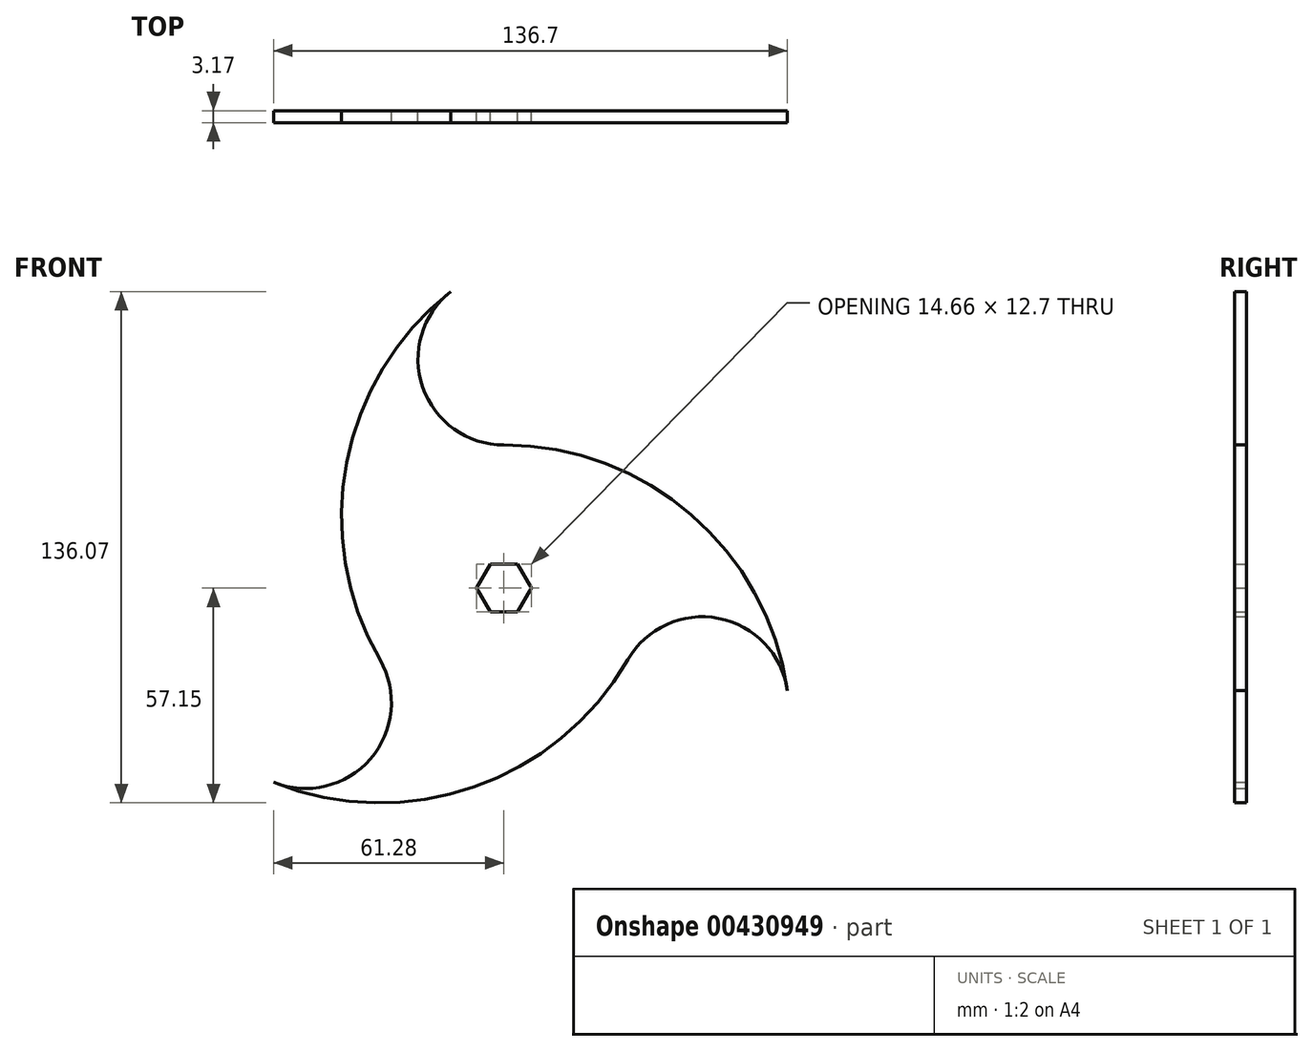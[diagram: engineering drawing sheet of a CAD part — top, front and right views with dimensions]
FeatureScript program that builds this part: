
annotation { "Feature Type Name" : "Feature", "Feature Type Description" : "" }
export const myFeature = defineFeature(function(context is Context, id is Id, definition is map)
    precondition{}
    {
        {
            var Q0;
            Q0=qCreatedBy(makeId("Front.planeOp"),FACE);
            var sketch = newSketch(context, id + "F0", { "sketchPlane" : qUnion([Q0])});
            skCircle(sketch, "E0.cCircle", {"center": v(0, 0) * mm, "radius": 6.35 * mm, "construction": true});
            skLineSegment(sketch, "E0.0", {"start": v(7.33, 0) * mm, "end": v(3.67, -6.35) * mm});
            skLineSegment(sketch, "E0.1", {"start": v(3.67, -6.35) * mm, "end": v(-3.67, -6.35) * mm});
            skLineSegment(sketch, "E0.2", {"start": v(-3.67, -6.35) * mm, "end": v(-7.33, 0) * mm});
            skLineSegment(sketch, "E0.3", {"start": v(-7.33, 0) * mm, "end": v(-3.67, 6.35) * mm});
            skLineSegment(sketch, "E0.4", {"start": v(-3.67, 6.35) * mm, "end": v(3.67, 6.35) * mm});
            skLineSegment(sketch, "E0.5", {"start": v(3.67, 6.35) * mm, "end": v(7.33, 0) * mm});
            skPoint(sketch, "E0.0.midPoint", {"position": v(5.5, -3.18) * mm});
            skCircle(sketch, "E1", {"center": v(0, 0) * mm, "radius": 38.1 * mm});
            skCircle(sketch, "E2.cCircle", {"center": v(0, 0) * mm, "radius": 38.1 * mm, "construction": true});
            skLineSegment(sketch, "E2.0", {"start": v(33, -19.05) * mm, "end": v(-33, -19.05) * mm, "construction": true});
            skLineSegment(sketch, "E2.1", {"start": v(-33, -19.05) * mm, "end": v(0, 38.1) * mm, "construction": true});
            skLineSegment(sketch, "E2.2", {"start": v(0, 38.1) * mm, "end": v(33, -19.05) * mm, "construction": true});
            skCircle(sketch, "E3", {"center": v(0, -38.1) * mm, "radius": 76.2 * mm});
            skCircle(sketch, "E4", {"center": v(52.8, -30.48) * mm, "radius": 22.86 * mm});
            skCircle(sketch, "E5.1.0", {"center": v(0, 60.96) * mm, "radius": 22.86 * mm});
            skCircle(sketch, "E5.1.1", {"center": v(33, 19.05) * mm, "radius": 76.2 * mm});
            skCircle(sketch, "E5.2.0", {"center": v(-52.8, -30.48) * mm, "radius": 22.86 * mm});
            skCircle(sketch, "E5.2.1", {"center": v(-33, 19.05) * mm, "radius": 76.2 * mm});
            skSolve(sketch);
        }
        {
            var Q0;
            {var subQ0=sQuery(id+"F0.wireOp",EDGE,"E5.1.0");var subQ1=sQuery(id+"F0.wireOp",EDGE,"E1");var subQ2=makeQuery(id+"F0.imprint","INTERSECT",VERTEX,{"derivedFrom":[subQ1,subQ0]});Q0=makeQuery(id+"F0.imprint","IMPRINT",FACE,{"disambiguationData":[TD([[makeQuery(id+"F0.imprint","IMPRINT",EDGE,{"disambiguationData":[TD([[subQ2,-1.0]])],"derivedFrom":subQ1}),-1.0]])]});}
            var Q1;
            {var subQ0=sQuery(id+"F0.wireOp",EDGE,"E5.2.0");var subQ1=sQuery(id+"F0.wireOp",EDGE,"E1");var subQ2=makeQuery(id+"F0.imprint","INTERSECT",VERTEX,{"derivedFrom":[subQ1,subQ0]});Q1=makeQuery(id+"F0.imprint","IMPRINT",FACE,{"disambiguationData":[TD([[makeQuery(id+"F0.imprint","IMPRINT",EDGE,{"disambiguationData":[TD([[subQ2,-1.0]])],"derivedFrom":subQ1}),-1.0]])]});}
            var Q2;
            {var subQ0=sQuery(id+"F0.wireOp",EDGE,"E3");var subQ1=sQuery(id+"F0.wireOp",EDGE,"E1");var subQ2=makeQuery(id+"F0.imprint","INTERSECT",VERTEX,{"derivedFrom":[subQ1,subQ0]});Q2=makeQuery(id+"F0.imprint","IMPRINT",FACE,{"disambiguationData":[TD([[makeQuery(id+"F0.imprint","IMPRINT",EDGE,{"disambiguationData":[TD([[subQ2,1.0]])],"derivedFrom":subQ1}),-1.0]])]});}
            var Q3;
            Q3=makeQuery(id+"F0.imprint","IMPRINT",FACE,{"disambiguationData":[TD([[makeQuery(id+"F0.imprint","IMPRINT",EDGE,{"derivedFrom":sQuery(id+"F0.wireOp",EDGE,"E0.0")}),1.0]])]});
            var Q4;
            {var subQ0=sQuery(id+"F0.wireOp",EDGE,"E5.1.0");var subQ1=sQuery(id+"F0.wireOp",EDGE,"E3");var subQ2=makeQuery(id+"F0.imprint","INTERSECT",VERTEX,{"disambiguationData":[OD(1.0)],"derivedFrom":[subQ1,subQ0]});Q4=makeQuery(id+"F0.imprint","IMPRINT",FACE,{"disambiguationData":[TD([[makeQuery(id+"F0.imprint","IMPRINT",EDGE,{"disambiguationData":[TD([[subQ2,-1.0]])],"derivedFrom":subQ1}),-1.0]])]});}
            var Q5;
            {var subQ0=sQuery(id+"F0.wireOp",EDGE,"E4");var subQ1=sQuery(id+"F0.wireOp",EDGE,"E3");var subQ2=makeQuery(id+"F0.imprint","INTERSECT",VERTEX,{"derivedFrom":[subQ1,subQ0]});Q5=makeQuery(id+"F0.imprint","IMPRINT",FACE,{"disambiguationData":[TD([[makeQuery(id+"F0.imprint","IMPRINT",EDGE,{"disambiguationData":[TD([[subQ2,-1.0]])],"derivedFrom":subQ1}),1.0]])]});}
            var Q6;
            {var subQ0=sQuery(id+"F0.wireOp",EDGE,"E5.2.0");var subQ1=sQuery(id+"F0.wireOp",EDGE,"E5.1.1");var subQ2=makeQuery(id+"F0.imprint","INTERSECT",VERTEX,{"disambiguationData":[OD(1.0)],"derivedFrom":[subQ1,subQ0]});Q6=makeQuery(id+"F0.imprint","IMPRINT",FACE,{"disambiguationData":[TD([[makeQuery(id+"F0.imprint","IMPRINT",EDGE,{"disambiguationData":[TD([[subQ2,-1.0]])],"derivedFrom":subQ1}),-1.0]])]});}
            extrude(context, id + "F1", {"entities" : qUnion([Q0, Q1, Q2, Q3, Q4, Q5, Q6]), "depth" : 3.17 * mm});
        }
    });
